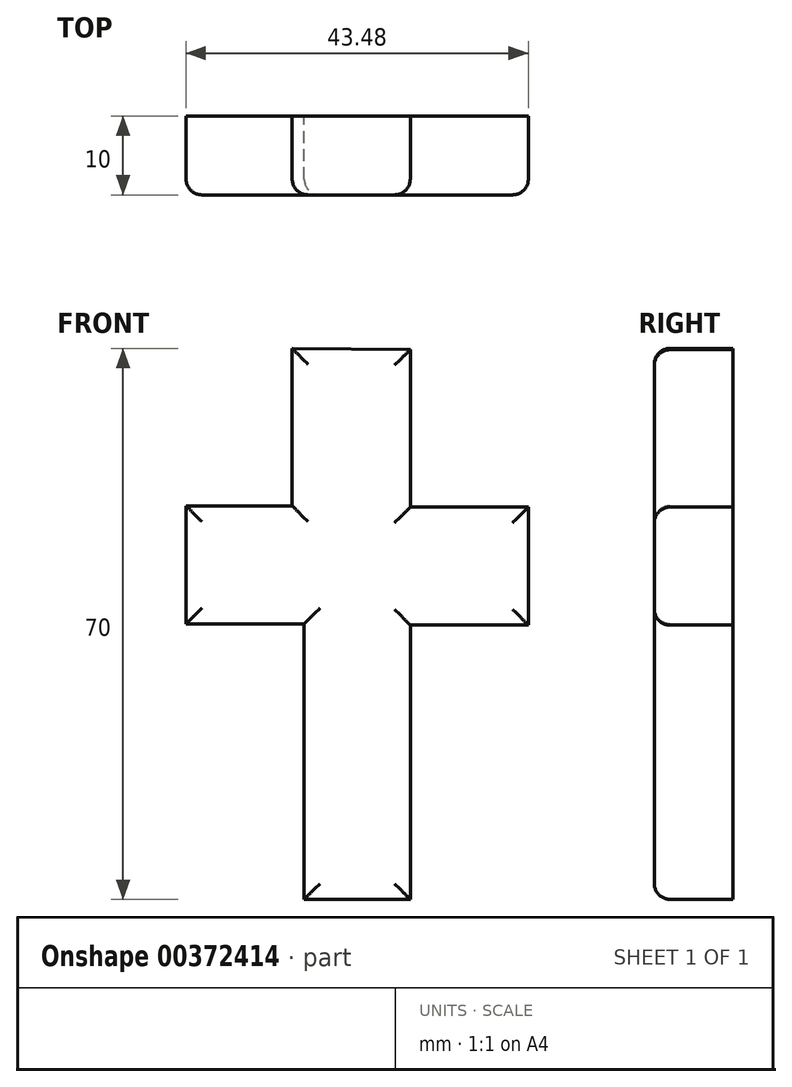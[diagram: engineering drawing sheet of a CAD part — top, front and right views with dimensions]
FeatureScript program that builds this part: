
annotation { "Feature Type Name" : "Feature", "Feature Type Description" : "" }
export const myFeature = defineFeature(function(context is Context, id is Id, definition is map)
    precondition{}
    {
        {
            var Q0;
            Q0=qCreatedBy(makeId("Front.planeOp"),FACE);
            var sketch = newSketch(context, id + "F0", { "sketchPlane" : qUnion([Q0])});
            skLineSegment(sketch, "E0", {"start": v(-15, 26.32) * mm, "end": v(-15, 6.32) * mm});
            skLineSegment(sketch, "E1", {"start": v(-15, 6.32) * mm, "end": v(-28.48, 6.32) * mm});
            skLineSegment(sketch, "E2", {"start": v(-28.48, 6.32) * mm, "end": v(-28.48, -8.68) * mm});
            skLineSegment(sketch, "E3", {"start": v(-28.48, -8.68) * mm, "end": v(-13.48, -8.68) * mm});
            skLineSegment(sketch, "E4", {"start": v(-13.48, -8.68) * mm, "end": v(-13.48, -43.68) * mm});
            skLineSegment(sketch, "E5", {"start": v(-13.48, -43.68) * mm, "end": v(0, -43.68) * mm});
            skLineSegment(sketch, "E6", {"start": v(0, -43.68) * mm, "end": v(0, -8.84) * mm});
            skLineSegment(sketch, "E7", {"start": v(0, -8.84) * mm, "end": v(15, -8.84) * mm});
            skLineSegment(sketch, "E8", {"start": v(15, -8.84) * mm, "end": v(15, 6.16) * mm});
            skLineSegment(sketch, "E9", {"start": v(15, 6.16) * mm, "end": v(0, 6.16) * mm});
            skLineSegment(sketch, "E10", {"start": v(0, 6.16) * mm, "end": v(0, 26.16) * mm});
            skLineSegment(sketch, "E11", {"start": v(0, 26.16) * mm, "end": v(-15, 26.32) * mm});
            skSolve(sketch);
        }
        {
            var Q0;
            Q0 = qSketchRegion(id + "F0", true);
            extrude(context, id + "F1", {"entities" : qUnion([Q0]), "depth" : 10 * mm});
        }
        {
            var Q0;
            Q0=makeQuery(id+"F1.opExtrude","CAP_FACE",FACE,{"disambiguationData":[OSD([sQuery(id+"F0.wireOp",EDGE,"E0"),sQuery(id+"F0.wireOp",EDGE,"E1"),sQuery(id+"F0.wireOp",EDGE,"E2"),sQuery(id+"F0.wireOp",EDGE,"E3"),sQuery(id+"F0.wireOp",EDGE,"E4"),sQuery(id+"F0.wireOp",EDGE,"E5"),sQuery(id+"F0.wireOp",EDGE,"E6"),sQuery(id+"F0.wireOp",EDGE,"E7"),sQuery(id+"F0.wireOp",EDGE,"E8"),sQuery(id+"F0.wireOp",EDGE,"E9"),sQuery(id+"F0.wireOp",EDGE,"E10"),sQuery(id+"F0.wireOp",EDGE,"E11")])],"isStart":false});
            fillet(context, id + "F2", {"entities" : qUnion([Q0]), "radius" : 2 * mm, "tangentPropagation" : true, "allowEdgeOverflow" : false});
        }
    });
